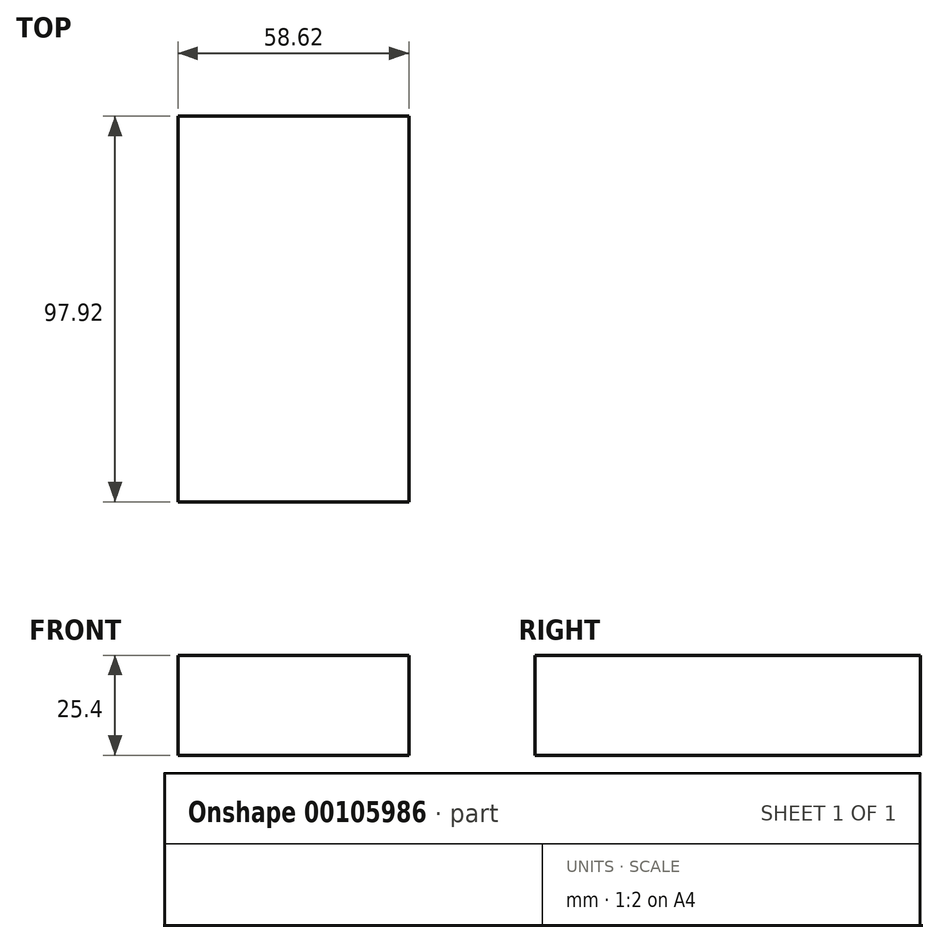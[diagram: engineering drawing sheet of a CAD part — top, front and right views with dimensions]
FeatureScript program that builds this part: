
annotation { "Feature Type Name" : "Feature", "Feature Type Description" : "" }
export const myFeature = defineFeature(function(context is Context, id is Id, definition is map)
    precondition{}
    {
        {
            var Q0;
            Q0=qCreatedBy(makeId("Top.planeOp"),FACE);
            var sketch = newSketch(context, id + "F0", { "sketchPlane" : qUnion([Q0])});
            skLineSegment(sketch, "E0.bottom", {"start": v(-22.46, -45.91) * mm, "end": v(36.16, -45.91) * mm});
            skLineSegment(sketch, "E0.top", {"start": v(-22.46, 52) * mm, "end": v(36.16, 52) * mm});
            skLineSegment(sketch, "E0.left", {"start": v(-22.46, -45.91) * mm, "end": v(-22.46, 52) * mm});
            skLineSegment(sketch, "E0.right", {"start": v(36.16, -45.91) * mm, "end": v(36.16, 52) * mm});
            skSolve(sketch);
        }
        {
            var Q0;
            Q0 = qSketchRegion(id + "F0", true);
            extrude(context, id + "F1", {"entities" : qUnion([Q0]), "depth" : 25.4 * mm});
        }
    });
